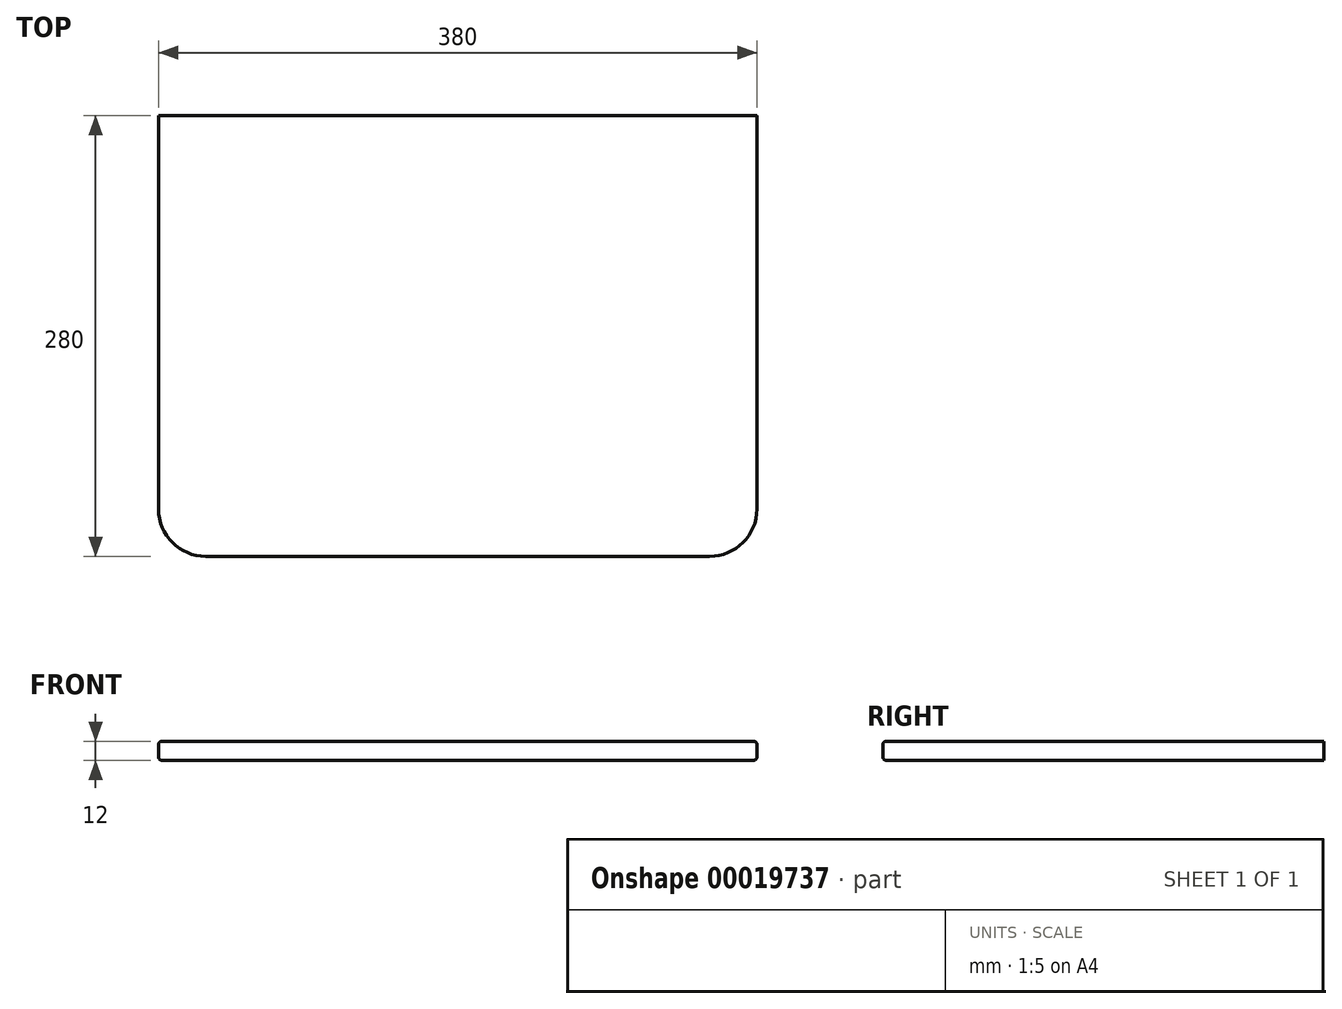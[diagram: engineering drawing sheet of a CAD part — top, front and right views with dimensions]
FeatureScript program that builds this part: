
annotation { "Feature Type Name" : "Feature", "Feature Type Description" : "" }
export const myFeature = defineFeature(function(context is Context, id is Id, definition is map)
    precondition{}
    {
        {
            var Q0;
            Q0=qCreatedBy(makeId("Top.planeOp"),FACE);
            var sketch = newSketch(context, id + "F0", { "sketchPlane" : qUnion([Q0])});
            skLineSegment(sketch, "E0.rect.bottom", {"start": v(190, 140) * mm, "end": v(-190, 140) * mm});
            skLineSegment(sketch, "E0.rect.top", {"start": v(190, -140) * mm, "end": v(-190, -140) * mm});
            skLineSegment(sketch, "E0.rect.left", {"start": v(190, 140) * mm, "end": v(190, -140) * mm});
            skLineSegment(sketch, "E0.rect.right", {"start": v(-190, 140) * mm, "end": v(-190, -140) * mm});
            skPoint(sketch, "E0.rect.middle", {"position": v(0, 0) * mm});
            skLineSegment(sketch, "E1.bottom", {"start": v(-190, 92.86) * mm, "end": v(-180, 92.86) * mm});
            skLineSegment(sketch, "E1.top", {"start": v(-190, -67.14) * mm, "end": v(-180, -67.14) * mm});
            skLineSegment(sketch, "E1.left", {"start": v(-190, 92.86) * mm, "end": v(-190, -67.14) * mm});
            skLineSegment(sketch, "E1.right", {"start": v(-180, 92.86) * mm, "end": v(-180, -67.14) * mm});
            skLineSegment(sketch, "E2.bottom", {"start": v(-147.7, -140) * mm, "end": v(148.78, -140) * mm});
            skLineSegment(sketch, "E2.top", {"start": v(-147.7, -130) * mm, "end": v(148.78, -130) * mm});
            skLineSegment(sketch, "E2.left", {"start": v(-147.7, -140) * mm, "end": v(-147.7, -130) * mm});
            skLineSegment(sketch, "E2.right", {"start": v(148.78, -140) * mm, "end": v(148.78, -130) * mm});
            skLineSegment(sketch, "E3", {"start": v(0, 0) * mm, "end": v(0, -194.99) * mm, "construction": true});
            skLineSegment(sketch, "E4.MirrorCS", {"start": v(190, 92.86) * mm, "end": v(190, -67.14) * mm});
            skLineSegment(sketch, "E5.bottom", {"start": v(190, 92.86) * mm, "end": v(180, 92.86) * mm});
            skLineSegment(sketch, "E5.top", {"start": v(190, -67.14) * mm, "end": v(180, -67.14) * mm});
            skLineSegment(sketch, "E5.right", {"start": v(180, 92.86) * mm, "end": v(180, -67.14) * mm});
            skSolve(sketch);
        }
        {
            var Q0;
            Q0 = qSketchRegion(id + "F0", true);
            extrude(context, id + "F1", {"entities" : qUnion([Q0]), "depth" : 12 * mm});
        }
        {
            var Q0;
            Q0=makeQuery(id+"F1.opExtrude","SWEPT_EDGE",EDGE,{"disambiguationData":[OSD([sQuery(id+"F0.wireOp",EDGE,"E0.rect.top"),sQuery(id+"F0.wireOp",EDGE,"E0.rect.left")])]});
            var Q1;
            Q1=makeQuery(id+"F1.opExtrude","SWEPT_EDGE",EDGE,{"disambiguationData":[OSD([sQuery(id+"F0.wireOp",EDGE,"E0.rect.top"),sQuery(id+"F0.wireOp",EDGE,"E0.rect.right")])]});
            fillet(context, id + "F2", {"entities" : qUnion([Q0, Q1]), "radius" : 30 * mm, "tangentPropagation" : true, "allowEdgeOverflow" : false});
        }
        {
            var Q0;
            Q0=makeQuery(id+"F1.opExtrude","CAP_EDGE",EDGE,{"disambiguationData":[OSD([sQuery(id+"F0.wireOp",EDGE,"E0.rect.top")])],"isStart":true});
            var Q1;
            Q1=makeQuery(id+"F1.opExtrude","CAP_EDGE",EDGE,{"disambiguationData":[OSD([sQuery(id+"F0.wireOp",EDGE,"E0.rect.top")])],"isStart":false});
            fillet(context, id + "F3", {"entities" : qUnion([Q0, Q1]), "radius" : 2 * mm, "tangentPropagation" : true, "allowEdgeOverflow" : false});
        }
    });
